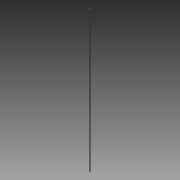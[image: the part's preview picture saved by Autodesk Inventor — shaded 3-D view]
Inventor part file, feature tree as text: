
AUTODESK INVENTOR PART (.ipt)
format: ipt  version: 2015 (Build 190159000, 159)  size: 65,024 bytes
history: native  units: in
note: dims shown in document units (in); Inventor stores cm internally (conversion verified against a paired STEP export)
features: extrude x1, thread x1, sketch x1
ambient origin geometry x8: Origin, YZ Plane, XZ Plane, XY Plane, X Axis, Y Axis, Z Axis, Center Point
bodies: Solid1 (feature_tree)
feature tree (3):
  extrude  "Extrusion1"  Depth=36.0in TaperAngle=0.0deg
  thread  "Thread1"  [1 undecoded]
  sketch  "Sketch1"  dims[d0=0.25in d1=36.0in d2=0.0in d3=1.0in d4=0.0in]
note: 1 required parameter value undecoded (feature->parameter linkage not recoverable at this tier; creation-order binding heuristic only, values carry confidence <= 0.55)
